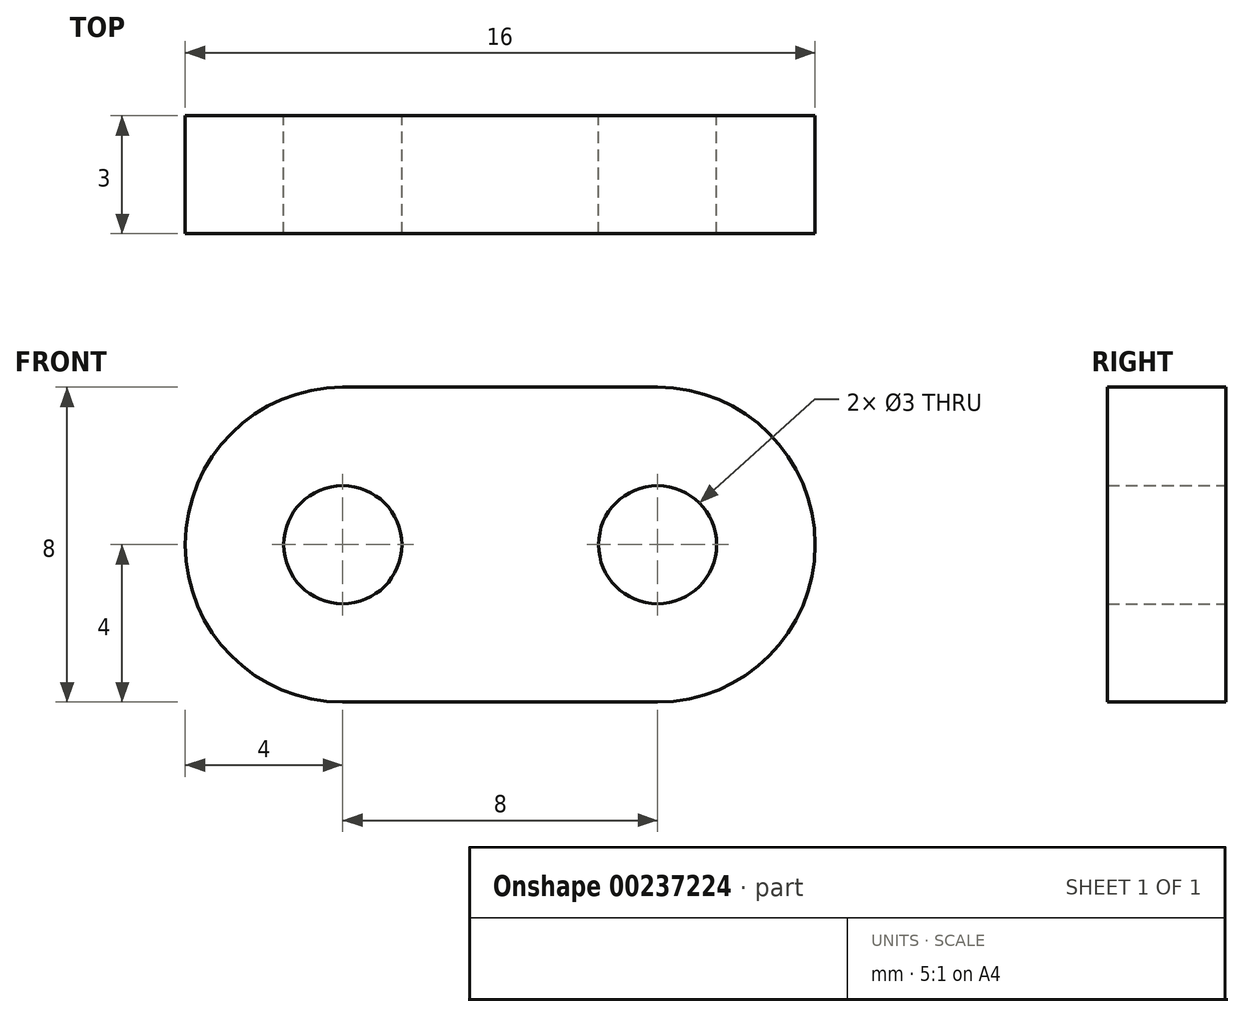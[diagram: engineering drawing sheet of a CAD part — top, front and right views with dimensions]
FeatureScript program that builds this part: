
annotation { "Feature Type Name" : "Feature", "Feature Type Description" : "" }
export const myFeature = defineFeature(function(context is Context, id is Id, definition is map)
    precondition{}
    {
        {
            var Q0;
            Q0=qCreatedBy(makeId("Front.planeOp"),FACE);
            var sketch = newSketch(context, id + "F0", { "sketchPlane" : qUnion([Q0])});
            skCircle(sketch, "E0", {"center": v(0, 0) * mm, "radius": 1.5 * mm});
            skLineSegment(sketch, "E1", {"start": v(0, 0) * mm, "end": v(8, 0) * mm});
            skCircle(sketch, "E2", {"center": v(8, 0) * mm, "radius": 1.5 * mm});
            skCircle(sketch, "E3", {"center": v(0, 0) * mm, "radius": 4 * mm});
            skCircle(sketch, "E4", {"center": v(8, 0) * mm, "radius": 4 * mm});
            skLineSegment(sketch, "E5", {"start": v(0, 4) * mm, "end": v(8, 4) * mm});
            skLineSegment(sketch, "E6", {"start": v(0, -4) * mm, "end": v(8, -4) * mm});
            skSolve(sketch);
        }
        {
            var Q0;
            Q0 = qSketchRegion(id + "F0", true);
            extrude(context, id + "F1", {"entities" : qUnion([Q0]), "depth" : 3 * mm});
        }
    });
